# Revit family: NBS_BetafenceLimited_MtlMeshPnlFncngSym_Securifor358-BekafixSuper
name_source: partatom
category: Site
revit_build: Autodesk Revit 2017 (Build: 20171027_0315(x64)
units: mm (PartAtom-declared; Revit-internal decimal feet)

## family parameters
Cut with Voids When Loaded = No
Part Type = Normal
Round Connector Dimension = Use Diameter
Shared = No

## types (1)
- Securifor 358 + Bekafix Super
    Applications = Warehouses, Distribution centres, power plants, laboratories, computer centres, financial institutions, military sites, penitentiaries, prisons
    AssetType = Fixed
    BIMObjectName = NBS_BetafenceLimited_MetalMeshPanelFencingSystem_Securifor358-BekafixSuper
    Category = Ss_25_14_67_51: Metal mesh panel fencing systems
    Color = Green (RAL 6005), black (RAL 9005)
    Description = Perimeter security
    Diameter = 0 mm  [stored 0 ft]
    DurationUnit = year
    Finish = Polyester coating
    FoundationMaterial = NBS_Concept
    Gradient01Maximum = 4.06%
    Gradient01PostAxisDistance = 2515 mm  [stored 8.25131 ft]
    Gradient02Maximum = 8.35%
    Gradient02PostAxisDistance = 2515 mm  [stored 8.25131 ft]
    Gradient03Maximum = 8.35%
    Gradient03PostAxisDistance = 2515 mm  [stored 8.25131 ft]
    Gradient04Maximum = 8.35%
    Gradient04PostAxisDistance = 2515 mm  [stored 8.25131 ft]
    GradientMaximumPostAxisDistance = 2515 mm  [stored 8.25131 ft]
    GradientStep = 4.06%
    Height = 3000 mm  [stored 9.84252 ft]
    IfcExportAs = IfcWallType
    IfcExportType = NOTDEFINED
    IsExternal = Yes
    ManufacturerName = Betafence Limited
    ManufacturerURL = www.betafence.co.uk
    MaximumIncline = 40.00%
    ModelReference = Securifor 358 Bekafix Super
    NBSCertification = www.nationalbimlibrary.com/cert/qpgwtvad
    NBSDescription = Metal mesh panel fencing system
    NBSReference = 25-20-30/145
    Name = MetalMeshPanelFencingSystem_Securifor358BekafixSuper_BetafenceLimited
    NominalHeight = 3000 mm  [stored 9.84252 ft]
    NominalLength = 0 mm  [stored 0 ft]
    NominalWidth = 2515 mm  [stored 8.25131 ft]
    PanelElevationAboveFoundation = 270 mm  [stored 0.885827 ft]
    PanelHeight = 3000 mm  [stored 9.84252 ft]
    PanelMaterial = NBS_BetafenceLimited_MtlMeshPnlFncngSym_Securifor358_Panel
    PanelOffsetFromPost = 12 mm  [stored 0.0393701 ft]
    PanelOffsetFromPostCL = 4 mm  [stored 0.0131234 ft]
    PanelSizeOptions = 2515 x 1270 mm, 2515 x 2400 mm, 2515 x 2700 mm, 2515 x 3000 mm, 2515 x 3300 mm, 2515 x 3600 mm, 2515 x 4000 mm, 2515 x 4500 mm, 2515 x 4800 mm, 2515 x 5200 mm
    PanelThickness = 7 mm  [stored 0.0229659 ft]
    Panels = PVC coating: hot dipped galvanised wire panels are sealed with an adhesion epoxy coating prior to the PVC coating to ensure a perfect bond zincalu super wire coating is a coating of (95%) zinc and (5%) aluminium which is highly recommended for coastal areas. (SANS 10244-2: 2004). weld strength of the wire (tensile range 540-690 N/m)
    PostFoundations = Installation guides available on request
    PostHeightAboveGround = 2800 mm  [stored 9.18635 ft]
    PostHeightBelowGround = 200 mm  [stored 0.656168 ft]
    PostMaterial = NBS_Concept
    PostThickness = 70 mm  [stored 0.229659 ft]
    PostWidth = 44 mm  [stored 0.144357 ft]
    Posts = Bekafix super
    ProductInformation = www.betafence.co.uk/en/securifor-358
    SecurityLevel = High and maximum security
    StandardPostAxisDistance = 2515 mm  [stored 8.25131 ft]
    SystemAccessories = Security fixation system: plastic coated metal clip with as an option stainless bolt with nut with break-off head, metal or polyamide fixing brackets, bekafix installation tongs, floor plate, connection piece to create bent arm for panels, single or double bent arms
    Uniclass2015Code = Ss_25_14_67_51
    Uniclass2015Title = Metal mesh panel fencing systems
    Uniclass2015Version = Systems v1.13
    Version = 2
    WarrantyDurationUnit = year

note: [stored X ft] marks values corroborated as IEEE doubles in the binary element streams (Revit-internal decimal feet)

## geometry (parser evidence)
native form markers: Sweep x6
no freeform markers — native parametric forms only
